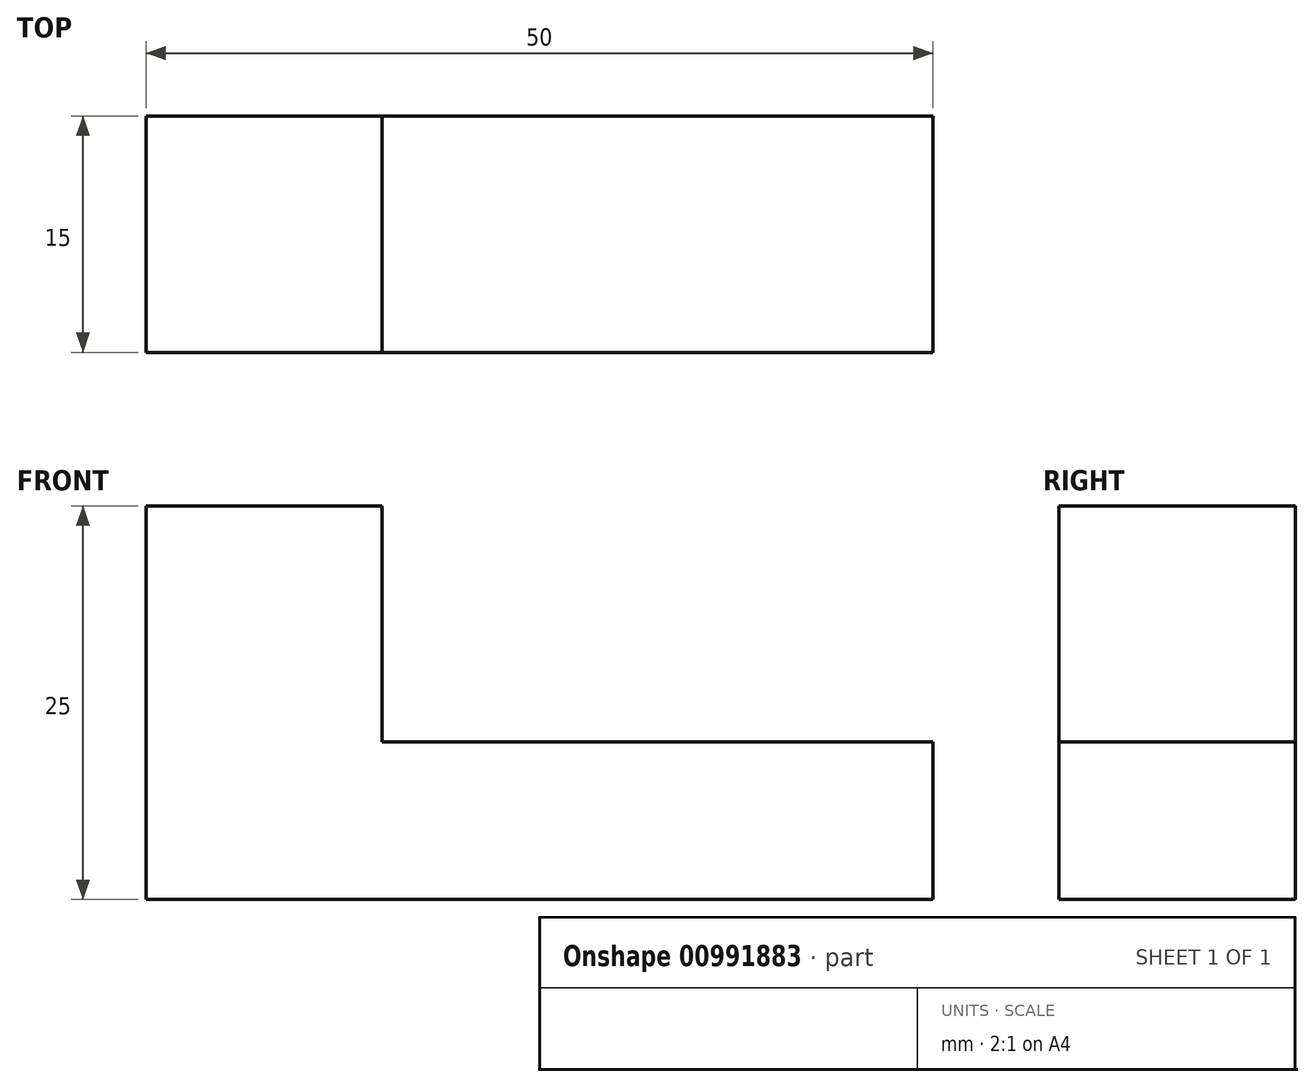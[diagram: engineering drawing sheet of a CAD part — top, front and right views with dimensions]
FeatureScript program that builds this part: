
annotation { "Feature Type Name" : "Feature", "Feature Type Description" : "" }
export const myFeature = defineFeature(function(context is Context, id is Id, definition is map)
    precondition{}
    {
        {
            var Q0;
            Q0=qCreatedBy(makeId("Front.planeOp"),FACE);
            var sketch = newSketch(context, id + "F0", { "sketchPlane" : qUnion([Q0])});
            skLineSegment(sketch, "E0.bottom", {"start": v(0, 0) * mm, "end": v(50, 0) * mm});
            skLineSegment(sketch, "E0.top", {"start": v(15, 10) * mm, "end": v(50, 10) * mm});
            skLineSegment(sketch, "E0.right", {"start": v(50, 0) * mm, "end": v(50, 10) * mm});
            skLineSegment(sketch, "E1.top", {"start": v(0, 25) * mm, "end": v(15, 25) * mm});
            skLineSegment(sketch, "E1.right", {"start": v(15, 10) * mm, "end": v(15, 25) * mm});
            skLineSegment(sketch, "E2", {"start": v(0, 0) * mm, "end": v(0, 25) * mm});
            skSolve(sketch);
        }
        {
            var Q0;
            Q0 = qSketchRegion(id + "F0", true);
            extrude(context, id + "F1", {"entities" : qUnion([Q0]), "depth" : 15 * mm, "offsetDistance" : 25 * mm});
        }
    });
